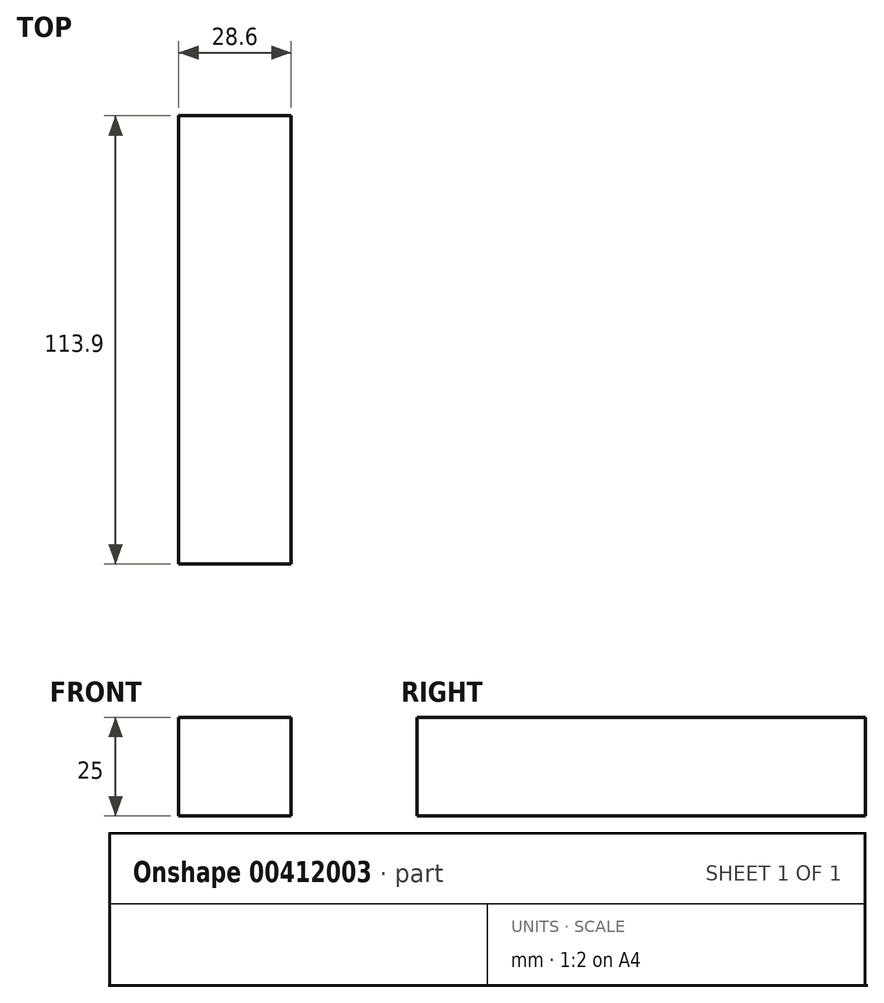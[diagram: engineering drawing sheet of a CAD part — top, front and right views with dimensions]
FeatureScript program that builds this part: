
annotation { "Feature Type Name" : "Feature", "Feature Type Description" : "" }
export const myFeature = defineFeature(function(context is Context, id is Id, definition is map)
    precondition{}
    {
        {
            var Q0;
            Q0=qCreatedBy(makeId("Top.planeOp"),FACE);
            var sketch = newSketch(context, id + "F0", { "sketchPlane" : qUnion([Q0])});
            skLineSegment(sketch, "E0.bottom", {"start": v(0, 0) * mm, "end": v(28.6, 0) * mm});
            skLineSegment(sketch, "E0.top", {"start": v(0, 113.9) * mm, "end": v(28.6, 113.9) * mm});
            skLineSegment(sketch, "E0.left", {"start": v(0, 0) * mm, "end": v(0, 113.9) * mm});
            skLineSegment(sketch, "E0.right", {"start": v(28.6, 0) * mm, "end": v(28.6, 113.9) * mm});
            skSolve(sketch);
        }
        {
            var Q0;
            Q0 = qBodyType(qCreatedBy(id + "F0" ,EDGE), BodyType.WIRE);
            var sketch = newSketch(context, id + "F1", { "sketchPlane" : qUnion([Q0])});
            skSolve(sketch);
        }
        {
            var Q0;
            Q0 = qSketchRegion(id + "F1", true);
            var Q1;
            Q1=makeQuery(id+"F0.imprint","IMPRINT",FACE,{"disambiguationData":[TD([[makeQuery(id+"F0.imprint","IMPRINT",EDGE,{"derivedFrom":sQuery(id+"F0.wireOp",EDGE,"E0.bottom")}),1.0]])]});
            extrude(context, id + "F2", {"entities" : qUnion([Q0, Q1]), "depth" : 25 * mm});
        }
    });
